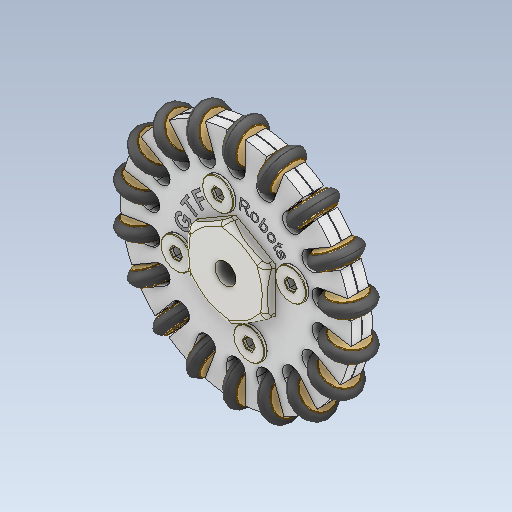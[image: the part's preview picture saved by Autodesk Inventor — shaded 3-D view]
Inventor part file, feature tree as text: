
AUTODESK INVENTOR PART (.ipt)
format: ipt  version: 2020 (Build 240168000, 168)  size: 3,832,320 bytes
history: native  units: mm
features: other x89, extrude x1, sketch x1
ambient origin geometry x8: Origin, YZ Plane, XZ Plane, XY Plane, X Axis, Y Axis, Z Axis, Center Point
bodies: Body2 (feature_tree), Body1 (feature_tree), Body3 (feature_tree), Body4 (feature_tree), Body5 (feature_tree), Body6 (feature_tree), Body7 (feature_tree), Body8 (feature_tree), Body9 (feature_tree), Body10 (feature_tree), Body11 (feature_tree), Body12 (feature_tree), Body13 (feature_tree), Body14 (feature_tree), Body15 (feature_tree), Body16 (feature_tree), Body17 (feature_tree), Body18 (feature_tree), Body19 (feature_tree), Body20 (feature_tree), Body21 (feature_tree), Body22 (feature_tree), Body23 (feature_tree), Body24 (feature_tree), Body25 (feature_tree), Body26 (feature_tree), Body27 (feature_tree), Body28 (feature_tree), Body29 (feature_tree), Body30 (feature_tree), Body31 (feature_tree), Body32 (feature_tree), Body33 (feature_tree), Body34 (feature_tree), Body35 (feature_tree), Body36 (feature_tree), Body37 (feature_tree), Body38 (feature_tree), Body39 (feature_tree), Body40 (feature_tree), Body41 (feature_tree), Body42 (feature_tree), Body43 (feature_tree), Body44 (feature_tree), Body45 (feature_tree), Body46 (feature_tree), Body47 (feature_tree), Body48 (feature_tree), Body49 (feature_tree), Body50 (feature_tree), Body51 (feature_tree), Body52 (feature_tree), Body53 (feature_tree), Body54 (feature_tree), Body55 (feature_tree), Body56 (feature_tree), Body57 (feature_tree), Body58 (feature_tree), Body59 (feature_tree), Body60 (feature_tree), Body61 (feature_tree), Body62 (feature_tree), Body63 (feature_tree), Body64 (feature_tree), Body65 (feature_tree), Body66 (feature_tree), Body67 (feature_tree), Body68 (feature_tree), Body69 (feature_tree), Body70 (feature_tree), Body71 (feature_tree), Body72 (feature_tree), Body73 (feature_tree), Body74 (feature_tree), Body75 (feature_tree), Body76 (feature_tree), Body77 (feature_tree), Body78 (feature_tree), Body79 (feature_tree), Body88 (feature_tree), Body89 (feature_tree), Body90 (feature_tree), Body91 (feature_tree), Body92 (feature_tree), Body93 (feature_tree), Body94 (feature_tree), Body95 (feature_tree), Body96 (feature_tree), Body97 (feature_tree)
feature tree (91):
  other  "Твердое тело1"
  extrude  "Выдавливание1"  Depth=4.0mm
  other  "Твердое тело2"
  other  "Твердое тело3"
  other  "Твердое тело4"
  other  "Твердое тело5"
  other  "Твердое тело6"
  other  "Твердое тело7"
  other  "Твердое тело8"
  other  "Твердое тело9"
  other  "Твердое тело10"
  other  "Твердое тело11"
  other  "Твердое тело12"
  other  "Твердое тело13"
  other  "Твердое тело14"
  other  "Твердое тело15"
  other  "Твердое тело16"
  other  "Твердое тело17"
  other  "Твердое тело18"
  other  "Твердое тело19"
  other  "Твердое тело20"
  other  "Твердое тело21"
  other  "Твердое тело22"
  other  "Твердое тело23"
  other  "Твердое тело24"
  other  "Твердое тело25"
  other  "Твердое тело26"
  other  "Твердое тело27"
  other  "Твердое тело28"
  other  "Твердое тело29"
  other  "Твердое тело30"
  other  "Твердое тело31"
  other  "Твердое тело32"
  other  "Твердое тело33"
  other  "Твердое тело34"
  other  "Твердое тело35"
  other  "Твердое тело36"
  other  "Твердое тело37"
  other  "Твердое тело38"
  other  "Твердое тело39"
  other  "Твердое тело40"
  other  "Твердое тело41"
  other  "Твердое тело42"
  other  "Твердое тело43"
  other  "Твердое тело44"
  other  "Твердое тело45"
  other  "Твердое тело46"
  other  "Твердое тело47"
  other  "Твердое тело48"
  other  "Твердое тело49"
  other  "Твердое тело50"
  other  "Твердое тело51"
  other  "Твердое тело52"
  other  "Твердое тело53"
  other  "Твердое тело54"
  other  "Твердое тело55"
  other  "Твердое тело56"
  other  "Твердое тело57"
  other  "Твердое тело58"
  other  "Твердое тело59"
  other  "Твердое тело60"
  other  "Твердое тело61"
  other  "Твердое тело62"
  other  "Твердое тело63"
  other  "Твердое тело64"
  other  "Твердое тело65"
  other  "Твердое тело66"
  other  "Твердое тело67"
  other  "Твердое тело68"
  other  "Твердое тело69"
  other  "Твердое тело70"
  other  "Твердое тело71"
  other  "Твердое тело72"
  other  "Твердое тело73"
  other  "Твердое тело74"
  other  "Твердое тело75"
  other  "Твердое тело76"
  other  "Твердое тело77"
  other  "Твердое тело78"
  other  "Твердое тело79"
  other  "Твердое тело80"
  other  "Твердое тело81"
  other  "Твердое тело82"
  other  "Твердое тело83"
  other  "Твердое тело84"
  other  "Твердое тело85"
  other  "Твердое тело86"
  other  "Твердое тело87"
  other  "Твердое тело88"
  other  "Твердое тело89"
  sketch  "Эскиз2"
